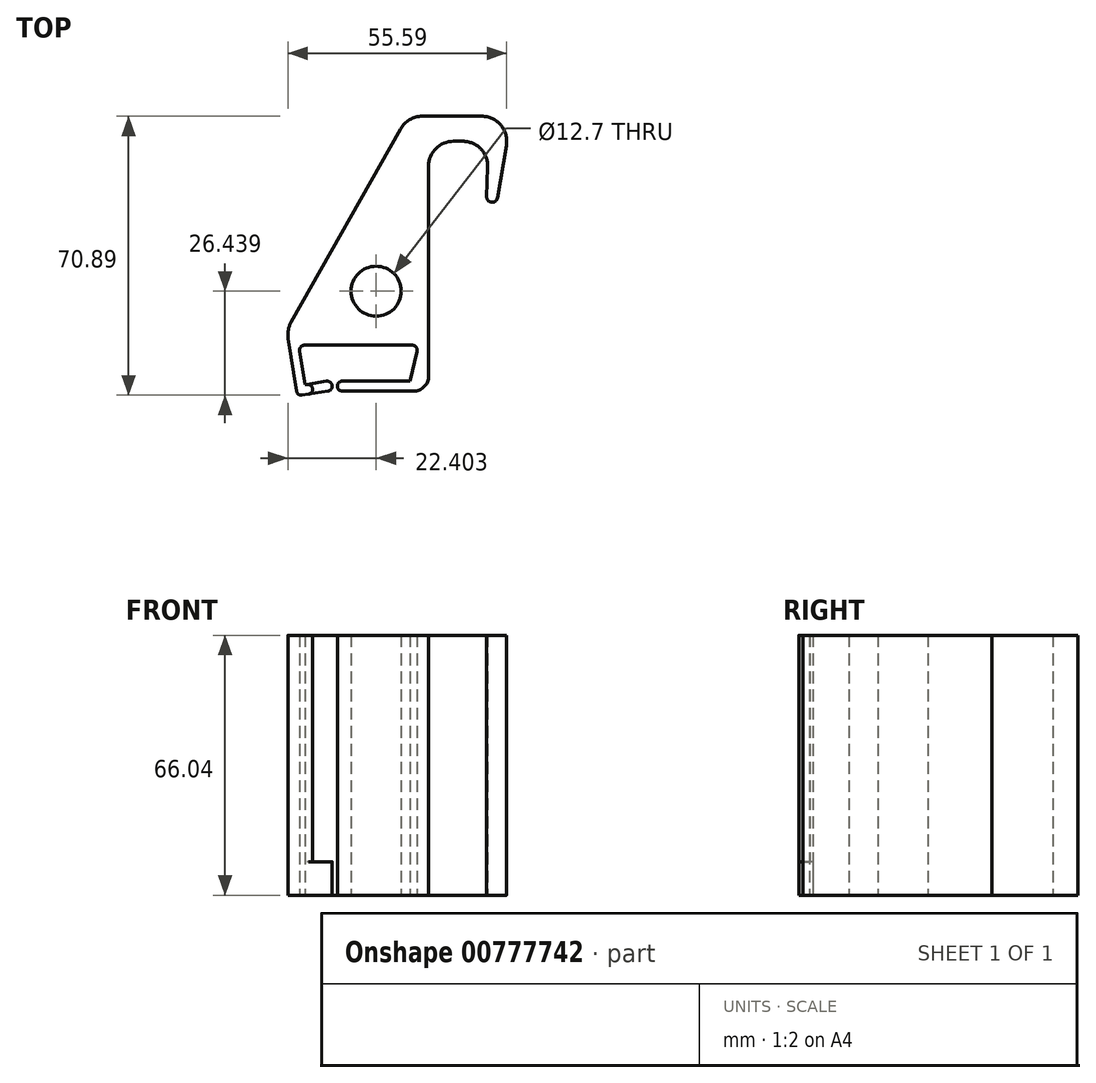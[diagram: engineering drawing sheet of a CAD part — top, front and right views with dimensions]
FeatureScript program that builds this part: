
annotation { "Feature Type Name" : "Feature", "Feature Type Description" : "" }
export const myFeature = defineFeature(function(context is Context, id is Id, definition is map)
    precondition{}
    {
        {
            var Q0;
            Q0=qCreatedBy(makeId("Top.planeOp"),FACE);
            var sketch = newSketch(context, id + "F0", { "sketchPlane" : qUnion([Q0])});
            skLineSegment(sketch, "E0", {"start": v(-21.1, -26.08) * mm, "end": v(-19.55, -25.83) * mm});
            skLineSegment(sketch, "E1", {"start": v(-18.5, -24.38) * mm, "end": v(-18.5, -24.38) * mm});
            skLineSegment(sketch, "E2", {"start": v(-19.94, -23.32) * mm, "end": v(-20.43, -23.4) * mm});
            skLineSegment(sketch, "E3", {"start": v(-20.43, -23.4) * mm, "end": v(-21.79, -14.84) * mm});
            skLineSegment(sketch, "E4", {"start": v(-20.53, -13.37) * mm, "end": v(6.84, -13.37) * mm});
            skLineSegment(sketch, "E5", {"start": v(8.08, -14.94) * mm, "end": v(6.24, -22.51) * mm});
            skLineSegment(sketch, "E6", {"start": v(6.24, -22.51) * mm, "end": v(-10.93, -22.51) * mm});
            skLineSegment(sketch, "E7", {"start": v(-12.2, -23.78) * mm, "end": v(-12.2, -23.78) * mm});
            skLineSegment(sketch, "E8", {"start": v(-10.93, -25.05) * mm, "end": v(7.19, -25.05) * mm});
            skLineSegment(sketch, "E9", {"start": v(11, -21.24) * mm, "end": v(11, 32.1) * mm});
            skLineSegment(sketch, "E10", {"start": v(17.35, 38.45) * mm, "end": v(19.67, 38.45) * mm});
            skLineSegment(sketch, "E11", {"start": v(26.02, 31.89) * mm, "end": v(25.77, 24.3) * mm});
            skLineSegment(sketch, "E12", {"start": v(24.5, 44.8) * mm, "end": v(9.38, 44.8) * mm});
            skLineSegment(sketch, "E13", {"start": v(-22.02, -13.37) * mm, "end": v(-40.43, -13.37) * mm, "construction": true});
            skLineSegment(sketch, "E14", {"start": v(30.76, 37.37) * mm, "end": v(28.44, 24) * mm});
            skLineSegment(sketch, "E15", {"start": v(26.95, 22.98) * mm, "end": v(26.79, 23) * mm});
            skLineSegment(sketch, "E16", {"start": v(6.24, -22.51) * mm, "end": v(-20.57, -22.51) * mm, "construction": true});
            skLineSegment(sketch, "E17", {"start": v(-22.55, -25.02) * mm, "end": v(-24.66, -11.65) * mm});
            skLineSegment(sketch, "E18", {"start": v(3.85, 41.58) * mm, "end": v(-23.92, -7.53) * mm});
            skPoint(sketch, "E19.visualSharp", {"position": v(5.67, 44.8) * mm});
            skArc(sketch, "E19.filletArc", {"start": v(9.38, 44.8) * mm, "mid": v(6.18, 43.93) * mm, "end": v(3.85, 41.58) * mm});
            skPoint(sketch, "E20.visualSharp", {"position": v(11, 38.45) * mm});
            skArc(sketch, "E20.filletArc", {"start": v(17.35, 38.45) * mm, "mid": v(12.86, 36.59) * mm, "end": v(11, 32.1) * mm});
            skPoint(sketch, "E21.visualSharp", {"position": v(26.24, 38.45) * mm});
            skArc(sketch, "E21.filletArc", {"start": v(26.02, 31.89) * mm, "mid": v(24.24, 36.51) * mm, "end": v(19.67, 38.45) * mm});
            skPoint(sketch, "E22.visualSharp", {"position": v(32.04, 44.8) * mm});
            skArc(sketch, "E22.filletArc", {"start": v(30.76, 37.37) * mm, "mid": v(29.36, 42.54) * mm, "end": v(24.5, 44.8) * mm});
            skPoint(sketch, "E23.visualSharp", {"position": v(-25.01, -9.46) * mm});
            skArc(sketch, "E23.filletArc", {"start": v(-23.92, -7.53) * mm, "mid": v(-24.64, -9.52) * mm, "end": v(-24.66, -11.65) * mm});
            skPoint(sketch, "E24.visualSharp", {"position": v(11, -25.05) * mm});
            skArc(sketch, "E24.filletArc", {"start": v(7.19, -25.05) * mm, "mid": v(9.88, -23.93) * mm, "end": v(11, -21.24) * mm});
            skPoint(sketch, "E25.visualSharp", {"position": v(-22.35, -26.28) * mm});
            skArc(sketch, "E25.filletArc", {"start": v(-22.55, -25.02) * mm, "mid": v(-22.04, -25.85) * mm, "end": v(-21.1, -26.08) * mm});
            skPoint(sketch, "E26.visualSharp", {"position": v(-22.02, -13.37) * mm});
            skArc(sketch, "E26.filletArc", {"start": v(-20.53, -13.37) * mm, "mid": v(-21.5, -13.81) * mm, "end": v(-21.79, -14.84) * mm});
            skPoint(sketch, "E27.visualSharp", {"position": v(8.46, -13.37) * mm});
            skArc(sketch, "E27.filletArc", {"start": v(8.08, -14.94) * mm, "mid": v(7.84, -13.85) * mm, "end": v(6.84, -13.37) * mm});
            skPoint(sketch, "E28.visualSharp", {"position": v(-12.2, -25.05) * mm});
            skArc(sketch, "E28.filletArc", {"start": v(-12.2, -23.78) * mm, "mid": v(-11.82, -24.68) * mm, "end": v(-10.93, -25.05) * mm});
            skPoint(sketch, "E29.visualSharp", {"position": v(-12.2, -22.51) * mm});
            skArc(sketch, "E29.filletArc", {"start": v(-10.93, -22.51) * mm, "mid": v(-11.82, -22.88) * mm, "end": v(-12.2, -23.78) * mm});
            skPoint(sketch, "E30.visualSharp", {"position": v(-18.69, -23.13) * mm});
            skArc(sketch, "E30.filletArc", {"start": v(-18.5, -24.38) * mm, "mid": v(-19, -23.55) * mm, "end": v(-19.94, -23.32) * mm});
            skPoint(sketch, "E31.visualSharp", {"position": v(-18.3, -25.63) * mm});
            skArc(sketch, "E31.filletArc", {"start": v(-19.55, -25.83) * mm, "mid": v(-18.72, -25.32) * mm, "end": v(-18.5, -24.38) * mm});
            skPoint(sketch, "E32.visualSharp", {"position": v(25.73, 23.22) * mm});
            skArc(sketch, "E32.filletArc", {"start": v(25.77, 24.3) * mm, "mid": v(26.04, 23.46) * mm, "end": v(26.79, 23) * mm});
            skPoint(sketch, "E33.visualSharp", {"position": v(28.22, 22.72) * mm});
            skArc(sketch, "E33.filletArc", {"start": v(26.95, 22.98) * mm, "mid": v(27.91, 23.18) * mm, "end": v(28.44, 24) * mm});
            skCircle(sketch, "E34", {"center": v(-2.34, 0.35) * mm, "radius": 6.35 * mm});
            skSolve(sketch);
        }
        {
            var Q0;
            Q0=makeQuery(id+"F0.imprint","IMPRINT",FACE,{"disambiguationData":[TD([[makeQuery(id+"F0.imprint","IMPRINT",EDGE,{"derivedFrom":sQuery(id+"F0.wireOp",EDGE,"E0")}),1.0]])]});
            extrude(context, id + "F1", {"entities" : qUnion([Q0]), "depth" : 66.04 * mm, "offsetDistance" : 25.4 * mm});
        }
        {
            var Q0;
            Q0=makeQuery(id+"F1.opExtrude","CAP_FACE",FACE,{"disambiguationData":[OSD([sQuery(id+"F0.wireOp",EDGE,"E0"),sQuery(id+"F0.wireOp",EDGE,"E2"),sQuery(id+"F0.wireOp",EDGE,"E3"),sQuery(id+"F0.wireOp",EDGE,"E4"),sQuery(id+"F0.wireOp",EDGE,"E5"),sQuery(id+"F0.wireOp",EDGE,"E6"),sQuery(id+"F0.wireOp",EDGE,"E8"),sQuery(id+"F0.wireOp",EDGE,"E9"),sQuery(id+"F0.wireOp",EDGE,"E10"),sQuery(id+"F0.wireOp",EDGE,"E11"),sQuery(id+"F0.wireOp",EDGE,"E12"),sQuery(id+"F0.wireOp",EDGE,"E14"),sQuery(id+"F0.wireOp",EDGE,"E15"),sQuery(id+"F0.wireOp",EDGE,"E17"),sQuery(id+"F0.wireOp",EDGE,"E18"),sQuery(id+"F0.wireOp",EDGE,"E19.filletArc"),sQuery(id+"F0.wireOp",EDGE,"E20.filletArc"),sQuery(id+"F0.wireOp",EDGE,"E21.filletArc"),sQuery(id+"F0.wireOp",EDGE,"E22.filletArc"),sQuery(id+"F0.wireOp",EDGE,"E23.filletArc"),sQuery(id+"F0.wireOp",EDGE,"E24.filletArc"),sQuery(id+"F0.wireOp",EDGE,"E25.filletArc"),sQuery(id+"F0.wireOp",EDGE,"E26.filletArc"),sQuery(id+"F0.wireOp",EDGE,"E27.filletArc"),sQuery(id+"F0.wireOp",EDGE,"E28.filletArc"),sQuery(id+"F0.wireOp",EDGE,"E29.filletArc"),sQuery(id+"F0.wireOp",EDGE,"E30.filletArc"),sQuery(id+"F0.wireOp",EDGE,"E31.filletArc"),sQuery(id+"F0.wireOp",EDGE,"E32.filletArc"),sQuery(id+"F0.wireOp",EDGE,"E33.filletArc"),sQuery(id+"F0.wireOp",EDGE,"E34")])],"isStart":true});
            var sketch = newSketch(context, id + "F2", { "sketchPlane" : qUnion([Q0])});
            skLineSegment(sketch, "E35", {"start": v(-20.43, 23.4) * mm, "end": v(-20.04, 25.91) * mm});
            skLineSegment(sketch, "E36", {"start": v(-20.04, 25.91) * mm, "end": v(-14.57, 25.04) * mm});
            skLineSegment(sketch, "E37", {"start": v(-13.51, 23.6) * mm, "end": v(-13.51, 23.6) * mm});
            skLineSegment(sketch, "E38", {"start": v(-14.97, 22.54) * mm, "end": v(-20.43, 23.4) * mm});
            skPoint(sketch, "E39.visualSharp", {"position": v(-13.31, 24.85) * mm});
            skArc(sketch, "E39.filletArc", {"start": v(-13.51, 23.6) * mm, "mid": v(-13.74, 24.54) * mm, "end": v(-14.57, 25.04) * mm});
            skPoint(sketch, "E40.visualSharp", {"position": v(-13.71, 22.34) * mm});
            skArc(sketch, "E40.filletArc", {"start": v(-14.97, 22.54) * mm, "mid": v(-14.02, 22.76) * mm, "end": v(-13.51, 23.6) * mm});
            skSolve(sketch);
        }
        {
            var Q0;
            {var subQ0=sQuery(id+"F2.wireOp",EDGE,"E39.filletArc");Q0=makeQuery(id+"F2.imprint","IMPRINT",FACE,{"disambiguationData":[TD([[makeQuery(id+"F2.imprint","IMPRINT",EDGE,{"derivedFrom":subQ0}),1.0]])]});}
            extrude(context, id + "F3", {"entities" : qUnion([Q0]), "operationType" : NewBodyOperationType.ADD, "oppositeDirection" : true, "depth" : 8.5 * mm, "offsetDistance" : 25.4 * mm});
        }
    });
